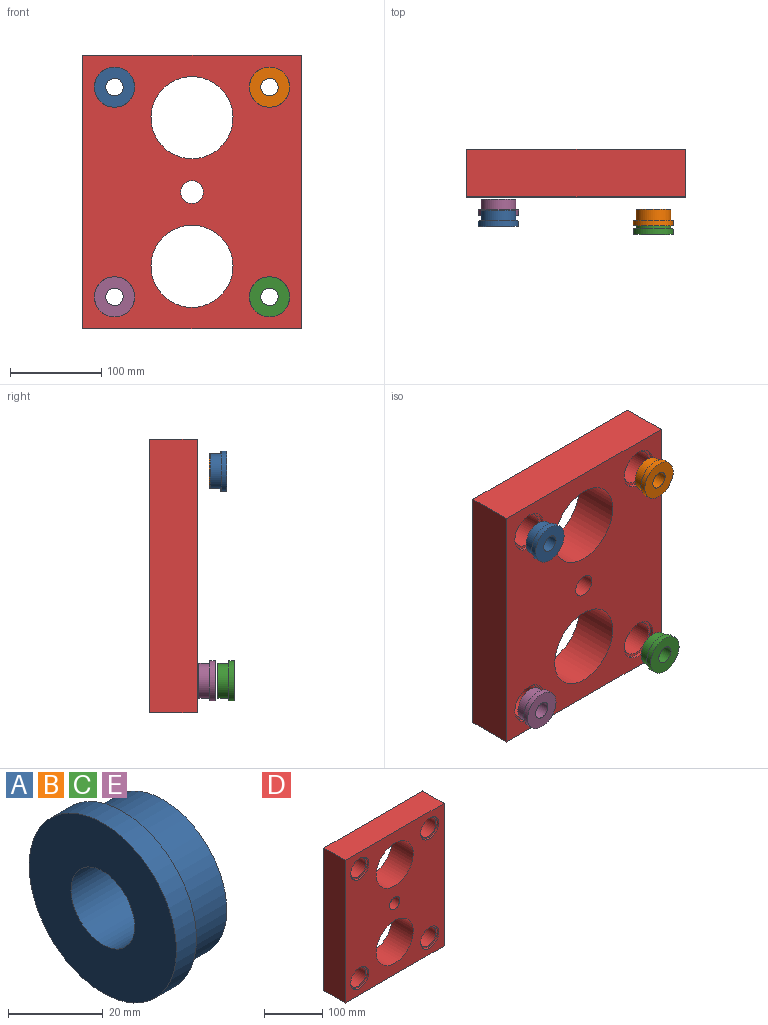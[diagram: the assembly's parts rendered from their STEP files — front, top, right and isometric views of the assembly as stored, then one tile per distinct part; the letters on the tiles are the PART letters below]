
ASSEMBLY  parts=5 mates=5
PART A: 6 faces, bbox 18x44x44 mm
  f0: cylinder r=9.52mm len=19.04mm, axis (-1,0,0), area 1076.7mm2, adj f1,f5
  f1: plane 44x44mm, normal (-1,0,0), area 1235.8mm2, adj f0,f2
  f2: cylinder r=22mm len=44mm, axis (-1,0,0), area 829.4mm2, adj f1,f3
  f3: plane 44x44mm, normal (1,0,0), area 380.4mm2, adj f2,f4
  f4: cylinder r=19.05mm len=38.1mm, axis (-1,0,0), area 1436.3mm2, adj f3,f5
  f5: plane 38.1x38.1mm, normal (1,0,0), area 855.4mm2, adj f0,f4
PART B: same geometry as A
PART C: same geometry as A
PART D: 21 faces, bbox 240x52x300 mm
  f0: plane 240x52mm, normal (0,0,1), area 12480mm2, adj f1,f4,f11,f12
  f1: plane 300x52mm, normal (-1,0,0), area 15600mm2, adj f0,f2,f11,f12
  f2: plane 240x52mm, normal (0,0,-1), area 12480mm2, adj f1,f4,f11,f12
  f3: cylinder r=12.5mm len=52mm, axis (0,1,0), area 4084.1mm2, adj f11,f12
  f4: plane 300x52mm, normal (1,0,0), area 15600mm2, adj f0,f2,f11,f12
  f5: cylinder r=22mm len=44mm, axis (0,1,0), area 552.9mm2, adj f11,f20
  f6: cylinder r=22mm len=44mm, axis (0,1,0), area 552.9mm2, adj f11,f14
  f7: cylinder r=45mm len=90mm, axis (0,1,0), area 14702.7mm2, adj f11,f12
  f8: cylinder r=22mm len=44mm, axis (0,1,0), area 552.9mm2, adj f11,f16
  f9: cylinder r=45mm len=90mm, axis (0,1,0), area 14702.7mm2, adj f11,f12
  f10: cylinder r=22mm len=44mm, axis (0,1,0), area 552.9mm2, adj f11,f18
  f11: plane 300x240mm, normal (0,-1,0), area 52703.6mm2, adj f0,f1,f2,f3,f4,f5,f6,f7
  f12: plane 300x240mm, normal (0,1,0), area 54225.3mm2, adj f0,f1,f2,f3,f4,f7,f9,f13
  f13: cylinder r=19.05mm len=48mm, axis (0,1,0), area 5745.3mm2, adj f12,f14
  f14: plane 44x44mm, normal (0,-1,0), area 380.4mm2, adj f6,f13
  f15: cylinder r=19.05mm len=48mm, axis (0,1,0), area 5745.3mm2, adj f12,f16
  f16: plane 44x44mm, normal (0,-1,0), area 380.4mm2, adj f8,f15
  f17: cylinder r=19.05mm len=48mm, axis (0,1,0), area 5745.3mm2, adj f12,f18
  f18: plane 44x44mm, normal (0,-1,0), area 380.4mm2, adj f10,f17
  f19: cylinder r=19.05mm len=48mm, axis (0,1,0), area 5745.3mm2, adj f12,f20
  f20: plane 44x44mm, normal (0,-1,0), area 380.4mm2, adj f5,f19
PART E: same geometry as A
PLACE A rot(axis=(0.58,0.58,0.58),120deg) t=(-527.47,-287.92,-550.85)mm
PLACE B rot(axis=(0.58,0.58,0.58),120deg) t=(-357.47,-287.07,-550.85)mm
PLACE C rot(axis=(0.58,0.58,0.58),120deg) t=(-357.47,-296.29,-780.85)mm
PLACE D t=(-667.03,-203.54,-647.08)mm
PLACE E rot(axis=(0.58,0.58,0.58),120deg) t=(-527.47,-275.44,-780.85)mm
MATE cylindrical B.f0 <-> D.f8  axis (0,-1,0) through (-357.47,-275.07,-550.85)mm
MATE slider C.f0 <-> D.f10  axis (0,-1,0) through (-357.47,-284.29,-780.85)mm
MATE cylindrical A.f0 <-> D.f5  axis (0,1,0) through (-527.47,-269.92,-550.85)mm
MATE cylindrical D.f6 <-> E.f0  axis (0,-1,0) through (-527.47,-251.54,-780.85)mm
MATE slider E.f0 <-> D.f6  axis (0,-1,0) through (-527.47,-269.44,-780.85)mm
